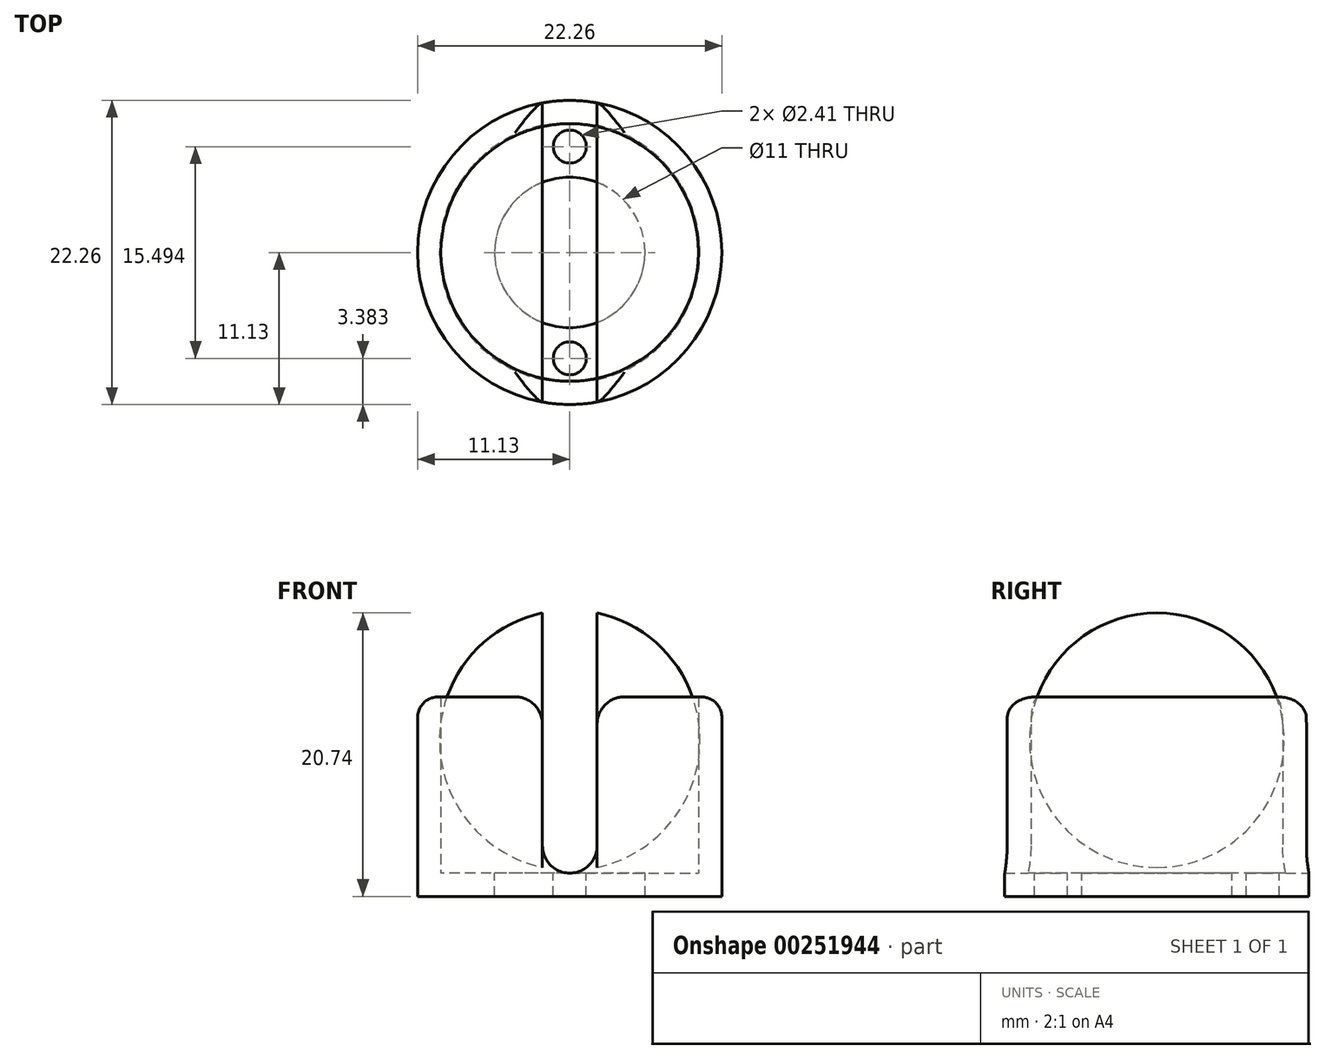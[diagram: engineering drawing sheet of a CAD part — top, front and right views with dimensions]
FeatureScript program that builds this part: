
annotation { "Feature Type Name" : "Feature", "Feature Type Description" : "" }
export const myFeature = defineFeature(function(context is Context, id is Id, definition is map)
    precondition{}
    {
        {
            var Q0;
            Q0=qCreatedBy(makeId("Front.planeOp"),FACE);
            var sketch = newSketch(context, id + "F0", { "sketchPlane" : qUnion([Q0])});
            skArc(sketch, "E0", {"start": v(0, -9.53) * mm, "mid": v(9.53, 0) * mm, "end": v(0, 9.53) * mm});
            skLineSegment(sketch, "E1", {"start": v(0, 17.81) * mm, "end": v(0, -25.05) * mm, "construction": true});
            skLineSegment(sketch, "E2", {"start": v(0, 9.53) * mm, "end": v(0, -9.53) * mm});
            skSolve(sketch);
        }
        {
            var Q0;
            Q0=makeQuery(id+"F0.imprint","IMPRINT",FACE,{"disambiguationData":[TD([[makeQuery(id+"F0.imprint","IMPRINT",EDGE,{"derivedFrom":sQuery(id+"F0.wireOp",EDGE,"E0")}),1.0]])]});
            var Q1;
            Q1=sQuery(id+"F0.wireOp",EDGE,"E1");
            revolve(context, id + "F1", {"entities" : qUnion([Q0]), "axis" : qUnion([Q1]), "revolveType" : RevolveType.FULL});
        }
        {
            var Q0;
            Q0=qCreatedBy(makeId("Top.planeOp"),FACE);
            cPlane(context, id + "F2", {"entities" : qUnion([Q0]), "cplaneType" : CPlaneType.OFFSET, "offset" : 11.43 * mm, "oppositeDirection" : true, "width" : 150 * mm, "height" : 150 * mm});
        }
        {
            var Q0;
            Q0=qCreatedBy(id+"F2.planeOp",FACE);
            var sketch = newSketch(context, id + "F3", { "sketchPlane" : qUnion([Q0])});
            skCircle(sketch, "E3", {"center": v(0, 0) * mm, "radius": 11.13 * mm});
            skSolve(sketch);
        }
        {
            var Q0;
            Q0 = qSketchRegion(id + "F3", true);
            extrude(context, id + "F4", {"entities" : qUnion([Q0]), "depth" : 14.6 * mm});
        }
        {
            var Q0;
            Q0=makeQuery(id+"F4.opExtrude","CAP_FACE",FACE,{"disambiguationData":[OSD([sQuery(id+"F3.wireOp",EDGE,"E3")])],"isStart":false});
            shell(context, id + "F5", {"entities" : qUnion([Q0]), "thickness" : 1.7 * mm});
        }
        {
            var Q0;
            Q0=qCreatedBy(makeId("Front.planeOp"),FACE);
            var sketch = newSketch(context, id + "F6", { "sketchPlane" : qUnion([Q0])});
            skLineSegment(sketch, "E4.bottom", {"start": v(2, -9.73) * mm, "end": v(-2, -9.73) * mm});
            skLineSegment(sketch, "E4.top", {"start": v(2, 9.73) * mm, "end": v(-2, 9.73) * mm});
            skLineSegment(sketch, "E4.left", {"start": v(2, -9.73) * mm, "end": v(2, 9.73) * mm});
            skLineSegment(sketch, "E4.right", {"start": v(-2, -9.73) * mm, "end": v(-2, 9.73) * mm});
            skPoint(sketch, "E4.middle", {"position": v(0, 0) * mm});
            skSolve(sketch);
        }
        {
            var Q0;
            Q0=makeQuery(id+"F6.imprint","IMPRINT",FACE,{"disambiguationData":[TD([[makeQuery(id+"F6.imprint","IMPRINT",EDGE,{"derivedFrom":sQuery(id+"F6.wireOp",EDGE,"E4.bottom")}),-1.0]])]});
            extrude(context, id + "F7", {"entities" : qUnion([Q0]), "operationType" : NewBodyOperationType.REMOVE, "endBound" : BoundingType.SYMMETRIC, "oppositeDirection" : true, "depth" : 25 * mm});
        }
        {
            var Q0;
            Q0=makeQuery(id+"F7.boolean.opBoolean","COPY",EDGE,{"disambiguationData":[OD(0.0)],"derivedFrom":makeQuery(id+"F7.opExtrude","SWEPT_EDGE",EDGE,{"disambiguationData":[OSD([sQuery(id+"F6.wireOp",EDGE,"E4.bottom"),sQuery(id+"F6.wireOp",EDGE,"E4.right")])]})});
            var Q1;
            Q1=makeQuery(id+"F7.boolean.opBoolean","COPY",EDGE,{"disambiguationData":[OD(1.0)],"derivedFrom":makeQuery(id+"F7.opExtrude","SWEPT_EDGE",EDGE,{"disambiguationData":[OSD([sQuery(id+"F6.wireOp",EDGE,"E4.bottom"),sQuery(id+"F6.wireOp",EDGE,"E4.right")])]})});
            var Q2;
            Q2=makeQuery(id+"F7.boolean.opBoolean","COPY",EDGE,{"disambiguationData":[OD(1.0)],"derivedFrom":makeQuery(id+"F7.opExtrude","SWEPT_EDGE",EDGE,{"disambiguationData":[OSD([sQuery(id+"F6.wireOp",EDGE,"E4.bottom"),sQuery(id+"F6.wireOp",EDGE,"E4.left")])]})});
            var Q3;
            Q3=makeQuery(id+"F7.boolean.opBoolean","COPY",EDGE,{"disambiguationData":[OD(0.0)],"derivedFrom":makeQuery(id+"F7.opExtrude","SWEPT_EDGE",EDGE,{"disambiguationData":[OSD([sQuery(id+"F6.wireOp",EDGE,"E4.bottom"),sQuery(id+"F6.wireOp",EDGE,"E4.left")])]})});
            var Q4;
            Q4=makeQuery(id+"F7.boolean.opBoolean","INTERSECT",EDGE,{"disambiguationData":[OD(0.0)],"derivedFrom":[makeQuery(id+"F4.opExtrude","CAP_FACE",FACE,{"disambiguationData":[OSD([sQuery(id+"F3.wireOp",EDGE,"E3")])],"isStart":false}),makeQuery(id+"F7.opExtrude","SWEPT_FACE",FACE,{"disambiguationData":[OSD([sQuery(id+"F6.wireOp",EDGE,"E4.right")])]})]});
            var Q5;
            Q5=makeQuery(id+"F7.boolean.opBoolean","INTERSECT",EDGE,{"disambiguationData":[OD(0.0)],"derivedFrom":[makeQuery(id+"F4.opExtrude","CAP_FACE",FACE,{"disambiguationData":[OSD([sQuery(id+"F3.wireOp",EDGE,"E3")])],"isStart":false}),makeQuery(id+"F7.opExtrude","SWEPT_FACE",FACE,{"disambiguationData":[OSD([sQuery(id+"F6.wireOp",EDGE,"E4.left")])]})]});
            var Q6;
            Q6=makeQuery(id+"F7.boolean.opBoolean","INTERSECT",EDGE,{"disambiguationData":[OD(1.0)],"derivedFrom":[makeQuery(id+"F4.opExtrude","CAP_FACE",FACE,{"disambiguationData":[OSD([sQuery(id+"F3.wireOp",EDGE,"E3")])],"isStart":false}),makeQuery(id+"F7.opExtrude","SWEPT_FACE",FACE,{"disambiguationData":[OSD([sQuery(id+"F6.wireOp",EDGE,"E4.right")])]})]});
            var Q7;
            Q7=makeQuery(id+"F7.boolean.opBoolean","INTERSECT",EDGE,{"disambiguationData":[OD(1.0)],"derivedFrom":[makeQuery(id+"F4.opExtrude","CAP_FACE",FACE,{"disambiguationData":[OSD([sQuery(id+"F3.wireOp",EDGE,"E3")])],"isStart":false}),makeQuery(id+"F7.opExtrude","SWEPT_FACE",FACE,{"disambiguationData":[OSD([sQuery(id+"F6.wireOp",EDGE,"E4.left")])]})]});
            fillet(context, id + "F8", {"entities" : qUnion([Q0, Q1, Q2, Q3, Q4, Q5, Q6, Q7]), "radius" : 2 * mm, "tangentPropagation" : true, "allowEdgeOverflow" : false});
        }
        {
            var Q0;
            {var subQ0=sQuery(id+"F3.wireOp",EDGE,"E3");Q0=makeQuery(id+"F7.boolean.opBoolean","SPLIT",EDGE,{"disambiguationData":[TD([makeQuery(id+"F7.opExtrude","SWEPT_FACE",FACE,{"disambiguationData":[OSD([sQuery(id+"F6.wireOp",EDGE,"E4.left")])]})])],"derivedFrom":makeQuery(id+"F4.opExtrude","CAP_EDGE",EDGE,{"disambiguationData":[OSD([subQ0])],"isStart":false})});}
            var Q1;
            {var subQ0=sQuery(id+"F3.wireOp",EDGE,"E3");Q1=makeQuery(id+"F7.boolean.opBoolean","SPLIT",EDGE,{"disambiguationData":[TD([makeQuery(id+"F7.opExtrude","SWEPT_FACE",FACE,{"disambiguationData":[OSD([sQuery(id+"F6.wireOp",EDGE,"E4.right")])]})])],"derivedFrom":makeQuery(id+"F4.opExtrude","CAP_EDGE",EDGE,{"disambiguationData":[OSD([subQ0])],"isStart":false})});}
            fillet(context, id + "F9", {"entities" : qUnion([Q0, Q1]), "radius" : 1.5 * mm, "allowEdgeOverflow" : false});
        }
        {
            var Q0;
            {var subQ0=sQuery(id+"F3.wireOp",EDGE,"E3");Q0=makeQuery(id+"F7.boolean.opBoolean","MERGE",FACE,{"derivedFrom":[makeQuery(id+"F5.opShell","OFFSET_FACE",FACE,{"disambiguationData":[OSD([subQ0]),TDD([makeQuery(id+"F4.opExtrude","CAP_FACE",FACE,{"disambiguationData":[OSD([subQ0])],"isStart":true})])]}),makeQuery(id+"F7.opExtrude","SWEPT_FACE",FACE,{"disambiguationData":[OSD([sQuery(id+"F6.wireOp",EDGE,"E4.bottom")])]})]});}
            var sketch = newSketch(context, id + "F10", { "sketchPlane" : qUnion([Q0])});
            skCircle(sketch, "E5", {"center": v(0, 0) * mm, "radius": 5.5 * mm});
            skLineSegment(sketch, "E6", {"start": v(0, -7.75) * mm, "end": v(0, 7.75) * mm, "construction": true});
            skCircle(sketch, "E7", {"center": v(0, -7.75) * mm, "radius": 1.2 * mm});
            skCircle(sketch, "E8", {"center": v(0, 7.75) * mm, "radius": 1.2 * mm});
            skSolve(sketch);
        }
        {
            var Q0;
            Q0=makeQuery(id+"F10.imprint","IMPRINT",FACE,{"disambiguationData":[TD([[makeQuery(id+"F10.imprint","IMPRINT",EDGE,{"derivedFrom":sQuery(id+"F10.wireOp",EDGE,"E7")}),1.0]])]});
            var Q1;
            Q1=makeQuery(id+"F10.imprint","IMPRINT",FACE,{"disambiguationData":[TD([[makeQuery(id+"F10.imprint","IMPRINT",EDGE,{"derivedFrom":sQuery(id+"F10.wireOp",EDGE,"E5")}),1.0]])]});
            var Q2;
            Q2=makeQuery(id+"F10.imprint","IMPRINT",FACE,{"disambiguationData":[TD([[makeQuery(id+"F10.imprint","IMPRINT",EDGE,{"derivedFrom":sQuery(id+"F10.wireOp",EDGE,"E8")}),1.0]])]});
            extrude(context, id + "F11", {"entities" : qUnion([Q0, Q1, Q2]), "operationType" : NewBodyOperationType.REMOVE, "oppositeDirection" : true, "depth" : 25 * mm});
        }
    });
